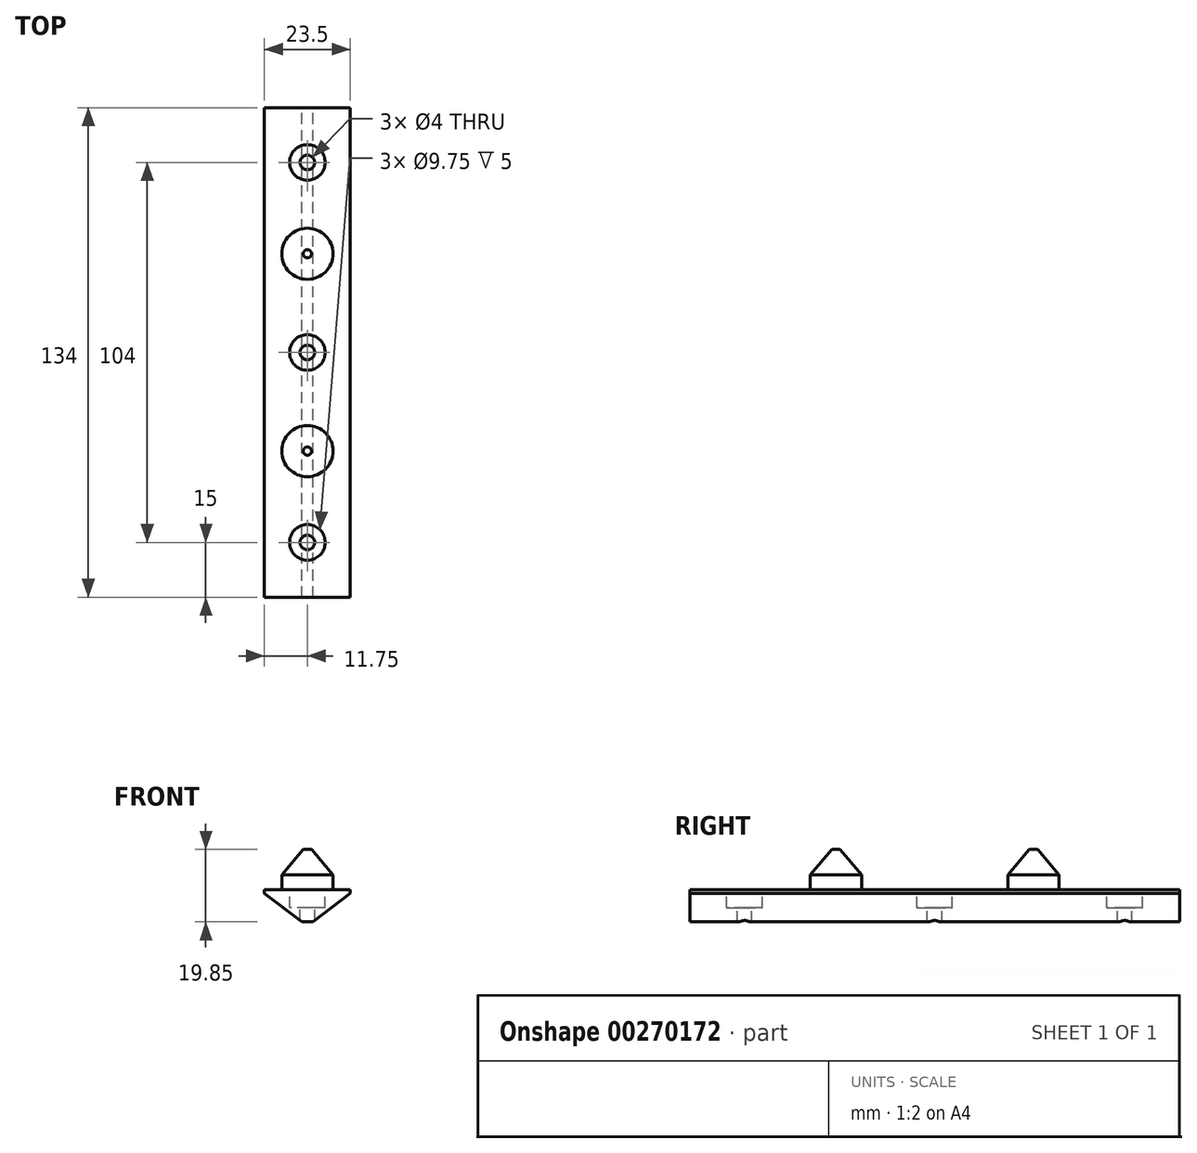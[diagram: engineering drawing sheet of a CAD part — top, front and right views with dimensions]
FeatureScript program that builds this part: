
annotation { "Feature Type Name" : "Feature", "Feature Type Description" : "" }
export const myFeature = defineFeature(function(context is Context, id is Id, definition is map)
    precondition{}
    {
        {
            var Q0;
            Q0=qCreatedBy(makeId("Front.planeOp"),FACE);
            var sketch = newSketch(context, id + "F0", { "sketchPlane" : qUnion([Q0])});
            skLineSegment(sketch, "E0", {"start": v(0, 0) * mm, "end": v(23.5, 0) * mm});
            skLineSegment(sketch, "E1", {"start": v(23.5, 0) * mm, "end": v(23.5, -1) * mm});
            skLineSegment(sketch, "E2", {"start": v(23.5, -1) * mm, "end": v(13.25, -8.85) * mm});
            skPoint(sketch, "E2.endSnap0", {"position": v(11.75, 0) * mm});
            skLineSegment(sketch, "E3", {"start": v(10.25, -8.85) * mm, "end": v(0, -1) * mm});
            skLineSegment(sketch, "E4", {"start": v(0, -1) * mm, "end": v(0, 0) * mm});
            skLineSegment(sketch, "E5", {"start": v(13.25, -8.85) * mm, "end": v(10.25, -8.85) * mm});
            skPoint(sketch, "E6.orphan", {"position": v(11.75, -10) * mm});
            skSolve(sketch);
        }
        {
            var Q0;
            Q0 = qSketchRegion(id + "F0", true);
            extrude(context, id + "F1", {"entities" : qUnion([Q0]), "depth" : 134 * mm});
        }
        {
            var Q0;
            Q0=makeQuery(id+"F1.opExtrude","SWEPT_FACE",FACE,{"disambiguationData":[OSD([sQuery(id+"F0.wireOp",EDGE,"E0")])]});
            var sketch = newSketch(context, id + "F2", { "sketchPlane" : qUnion([Q0])});
            skPoint(sketch, "E7", {"position": v(11.75, -15) * mm});
            skPoint(sketch, "E8", {"position": v(11.75, -67) * mm});
            skPoint(sketch, "E9", {"position": v(11.75, -119) * mm});
            skSolve(sketch);
        }
        {
            var Q0;
            Q0=sQuery(id+"F2.wireOp",VERTEX,"E7");
            var Q1;
            Q1=sQuery(id+"F2.wireOp",VERTEX,"E8");
            var Q2;
            Q2=sQuery(id+"F2.wireOp",VERTEX,"E9");
            var Q3;
            Q3=makeQuery(id+"F1.opExtrude","SWEPT_BODY",BODY,{"disambiguationData":[OSD([sQuery(id+"F0.wireOp",EDGE,"E0"),sQuery(id+"F0.wireOp",EDGE,"E1"),sQuery(id+"F0.wireOp",EDGE,"E2"),sQuery(id+"F0.wireOp",EDGE,"E3"),sQuery(id+"F0.wireOp",EDGE,"E4"),sQuery(id+"F0.wireOp",EDGE,"E5")])]});
            hole(context, id + "F3", {"style" : HoleStyle.C_BORE, "endStyle" : HoleEndStyle.THROUGH, "standardTappedOrClearance" : lookupTablePath({ "standard" : "ISO", "engagement" : "75%", "pitch" : "1 mm", "size" : "M5", "type" : "Tapped" }), "standardBlindInLast" : lookupTablePath({ "standard" : "ISO", "engagement" : "75%", "pitch" : "1 mm", "size" : "M5", "type" : "Tapped" }), "holeDiameter" : 4 * mm, "cBoreDiameter" : 9.75 * mm, "cBoreDepth" : 5 * mm, "showTappedDepth" : true, "tappedDepth" : 12 * mm, "tapClearance" : 3, "startFromSketch" : true, "locations" : qUnion([Q0, Q1, Q2]), "scope" : qUnion([Q3])});
        }
        {
            var Q0;
            Q0=makeQuery(id+"F1.opExtrude","SWEPT_FACE",FACE,{"disambiguationData":[OSD([sQuery(id+"F0.wireOp",EDGE,"E0")])]});
            var sketch = newSketch(context, id + "F4", { "sketchPlane" : qUnion([Q0])});
            skCircle(sketch, "E10", {"center": v(11.75, -40) * mm, "radius": 7 * mm});
            skCircle(sketch, "E11", {"center": v(11.75, -94) * mm, "radius": 7 * mm});
            skSolve(sketch);
        }
        {
            var Q0;
            Q0 = qSketchRegion(id + "F4", true);
            extrude(context, id + "F5", {"entities" : qUnion([Q0]), "operationType" : NewBodyOperationType.ADD, "depth" : 4 * mm, "hasDraft" : true, "draftAngle" : 0 * degree, "draftPullDirection" : true});
        }
        {
            var Q0;
            Q0=makeQuery(id+"F5.opExtrude","CAP_FACE",FACE,{"disambiguationData":[OSD([sQuery(id+"F4.wireOp",EDGE,"E10")])],"isStart":false});
            var sketch = newSketch(context, id + "F6", { "sketchPlane" : qUnion([Q0])});
            skCircle(sketch, "E12", {"center": v(11.75, -40) * mm, "radius": 7 * mm});
            skCircle(sketch, "E13", {"center": v(11.75, -94) * mm, "radius": 7 * mm});
            skSolve(sketch);
        }
        {
            var Q0;
            Q0 = qSketchRegion(id + "F6", true);
            extrude(context, id + "F7", {"entities" : qUnion([Q0]), "operationType" : NewBodyOperationType.ADD, "depth" : 7 * mm, "hasDraft" : true, "draftAngle" : 40 * degree, "draftPullDirection" : true});
        }
    });
